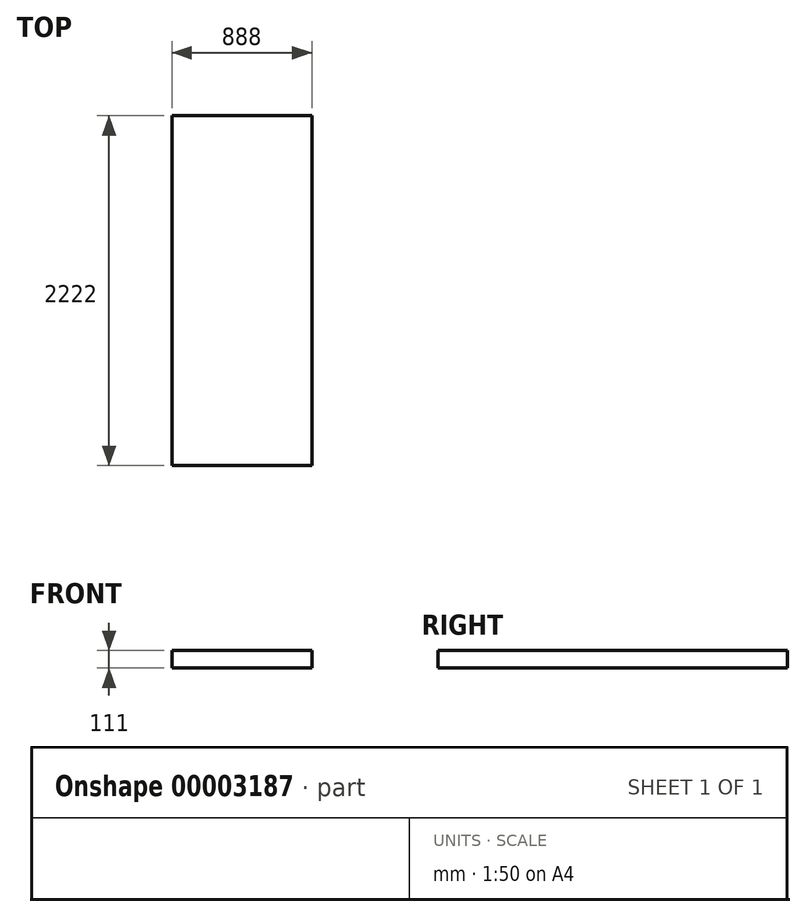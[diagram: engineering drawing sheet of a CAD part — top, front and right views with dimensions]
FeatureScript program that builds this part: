
annotation { "Feature Type Name" : "Feature", "Feature Type Description" : "" }
export const myFeature = defineFeature(function(context is Context, id is Id, definition is map)
    precondition{}
    {
        {
            var Q0;
            Q0=qCreatedBy(makeId("Top.planeOp"),FACE);
            var sketch = newSketch(context, id + "F0", { "sketchPlane" : qUnion([Q0])});
            skLineSegment(sketch, "E0.bottom", {"start": v(-444, 1111) * mm, "end": v(444, 1111) * mm});
            skLineSegment(sketch, "E0.top", {"start": v(-444, -1111) * mm, "end": v(444, -1111) * mm});
            skLineSegment(sketch, "E0.left", {"start": v(-444, 1111) * mm, "end": v(-444, -1111) * mm});
            skLineSegment(sketch, "E0.right", {"start": v(444, 1111) * mm, "end": v(444, -1111) * mm});
            skSolve(sketch);
        }
        {
            var Q0;
            Q0=makeQuery(id+"F0.imprint","IMPRINT",FACE,{"disambiguationData":[TD([[makeQuery(id+"F0.imprint","IMPRINT",EDGE,{"derivedFrom":sQuery(id+"F0.wireOp",EDGE,"E0.bottom")}),-1.0]])]});
            extrude(context, id + "F1", {"entities" : qUnion([Q0]), "oppositeDirection" : true, "depth" : 111 * mm});
        }
    });
